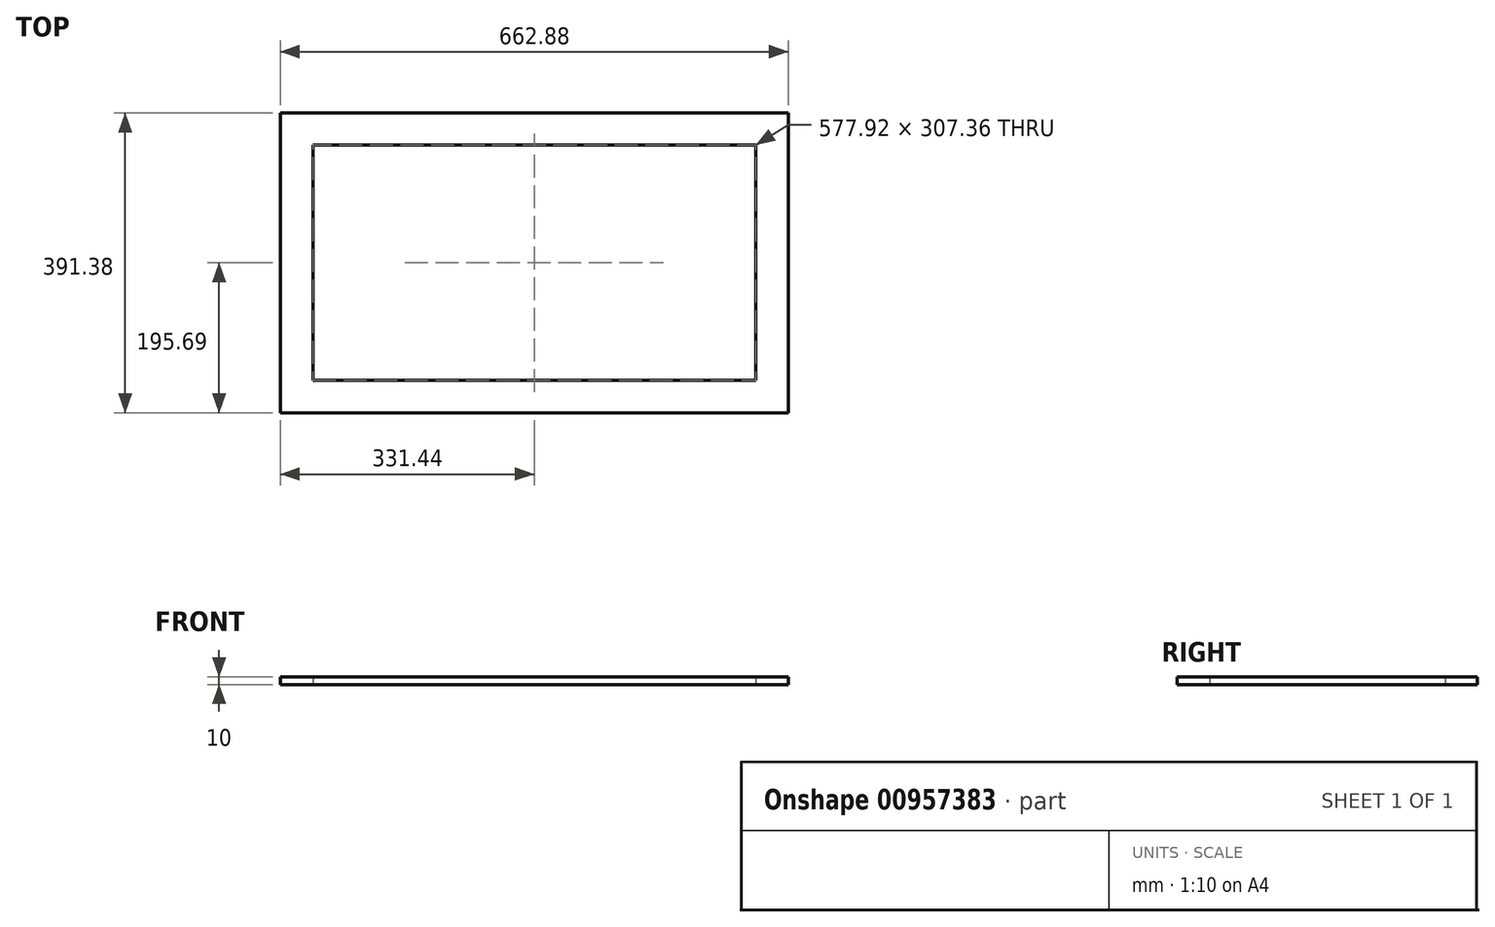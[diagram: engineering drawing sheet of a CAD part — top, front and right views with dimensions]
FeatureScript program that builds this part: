
annotation { "Feature Type Name" : "Feature", "Feature Type Description" : "" }
export const myFeature = defineFeature(function(context is Context, id is Id, definition is map)
    precondition{}
    {
        {
            var Q0;
            Q0=qCreatedBy(makeId("Top.planeOp"),FACE);
            var sketch = newSketch(context, id + "F0", { "sketchPlane" : qUnion([Q0])});
            skLineSegment(sketch, "E0.bottom", {"start": v(288.96, 153.68) * mm, "end": v(-288.96, 153.68) * mm});
            skLineSegment(sketch, "E0.top", {"start": v(288.96, -153.68) * mm, "end": v(-288.96, -153.68) * mm});
            skLineSegment(sketch, "E0.left", {"start": v(288.96, 153.68) * mm, "end": v(288.96, -153.68) * mm});
            skLineSegment(sketch, "E0.right", {"start": v(-288.96, 153.68) * mm, "end": v(-288.96, -153.68) * mm});
            skPoint(sketch, "E0.middle", {"position": v(0, 0) * mm});
            skLineSegment(sketch, "E1.bottom", {"start": v(331.44, -195.69) * mm, "end": v(-331.44, -195.69) * mm});
            skLineSegment(sketch, "E1.top", {"start": v(331.44, 195.69) * mm, "end": v(-331.44, 195.69) * mm});
            skLineSegment(sketch, "E1.left", {"start": v(331.44, -195.69) * mm, "end": v(331.44, 195.69) * mm});
            skLineSegment(sketch, "E1.right", {"start": v(-331.44, -195.69) * mm, "end": v(-331.44, 195.69) * mm});
            skSolve(sketch);
        }
        {
            var Q0;
            Q0 = qSketchRegion(id + "F0", true);
            extrude(context, id + "F1", {"entities" : qUnion([Q0]), "depth" : 10 * mm, "offsetDistance" : 25 * mm});
        }
    });
